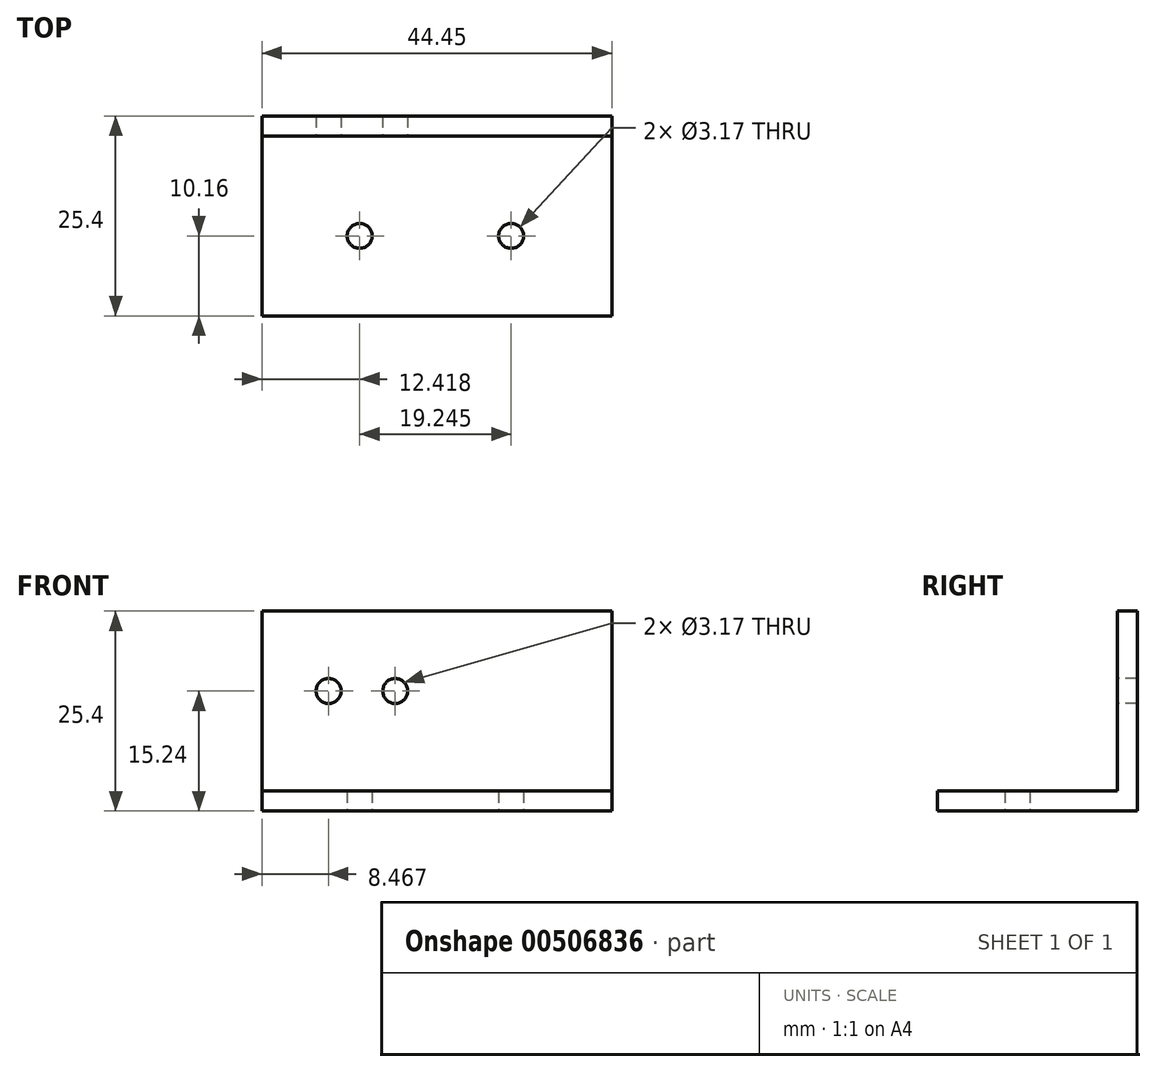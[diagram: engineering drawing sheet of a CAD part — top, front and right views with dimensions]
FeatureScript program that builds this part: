
annotation { "Feature Type Name" : "Feature", "Feature Type Description" : "" }
export const myFeature = defineFeature(function(context is Context, id is Id, definition is map)
    precondition{}
    {
        {
            var Q0;
            Q0=qCreatedBy(makeId("Top.planeOp"),FACE);
            var sketch = newSketch(context, id + "F0", { "sketchPlane" : qUnion([Q0])});
            skLineSegment(sketch, "E0.bottom", {"start": v(-44.45, -10.28) * mm, "end": v(0, -10.28) * mm});
            skLineSegment(sketch, "E0.top", {"start": v(-44.45, -35.68) * mm, "end": v(0, -35.68) * mm});
            skLineSegment(sketch, "E0.left", {"start": v(-44.45, -10.28) * mm, "end": v(-44.45, -35.68) * mm});
            skLineSegment(sketch, "E0.right", {"start": v(0, -10.28) * mm, "end": v(0, -35.68) * mm});
            skSolve(sketch);
        }
        {
            var Q0;
            Q0=makeQuery(id+"F0.imprint","IMPRINT",FACE,{"disambiguationData":[TD([[makeQuery(id+"F0.imprint","IMPRINT",EDGE,{"derivedFrom":sQuery(id+"F0.wireOp",EDGE,"E0.bottom")}),-1.0]])]});
            extrude(context, id + "F1", {"entities" : qUnion([Q0]), "depth" : 25.4 * mm, "offsetDistance" : 25.4 * mm});
        }
        {
            var Q0;
            Q0=makeQuery(id+"F1.opExtrude","CAP_FACE",FACE,{"disambiguationData":[OSD([sQuery(id+"F0.wireOp",EDGE,"E0.bottom"),sQuery(id+"F0.wireOp",EDGE,"E0.top"),sQuery(id+"F0.wireOp",EDGE,"E0.left"),sQuery(id+"F0.wireOp",EDGE,"E0.right")])],"isStart":false});
            var Q1;
            Q1=makeQuery(id+"F1.opExtrude","SWEPT_FACE",FACE,{"disambiguationData":[OSD([sQuery(id+"F0.wireOp",EDGE,"E0.right")])]});
            var Q2;
            Q2=makeQuery(id+"F1.opExtrude","SWEPT_FACE",FACE,{"disambiguationData":[OSD([sQuery(id+"F0.wireOp",EDGE,"E0.top")])]});
            var Q3;
            Q3=makeQuery(id+"F1.opExtrude","SWEPT_FACE",FACE,{"disambiguationData":[OSD([sQuery(id+"F0.wireOp",EDGE,"E0.left")])]});
            shell(context, id + "F2", {"entities" : qUnion([Q0, Q1, Q2, Q3]), "thickness" : 2.54 * mm});
        }
        {
            var Q0;
            Q0=makeQuery(id+"F2.opShell","OFFSET_FACE",FACE,{"disambiguationData":[OSD([sQuery(id+"F0.wireOp",EDGE,"E0.bottom")])]});
            var sketch = newSketch(context, id + "F3", { "sketchPlane" : qUnion([Q0])});
            skPoint(sketch, "E1", {"position": v(-27.52, 15.24) * mm});
            skPoint(sketch, "E2", {"position": v(-35.98, 15.24) * mm});
            skSolve(sketch);
        }
        {
            var Q0;
            Q0=sQuery(id+"F3.wireOp",VERTEX,"E2");
            var Q1;
            Q1=sQuery(id+"F3.wireOp",VERTEX,"E1");
            var Q2;
            Q2=makeQuery(id+"F1.opExtrude","SWEPT_BODY",BODY,{"disambiguationData":[OSD([sQuery(id+"F0.wireOp",EDGE,"E0.bottom"),sQuery(id+"F0.wireOp",EDGE,"E0.top"),sQuery(id+"F0.wireOp",EDGE,"E0.left"),sQuery(id+"F0.wireOp",EDGE,"E0.right")])]});
            hole(context, id + "F4", {"style" : HoleStyle.SIMPLE, "endStyle" : HoleEndStyle.THROUGH, "holeDiameter" : 3.17 * mm, "majorDiameter" : 6.35 * mm, "isTappedThrough" : true, "tappedDepth" : 12.7 * mm, "tapClearance" : 3, "locations" : qUnion([Q0, Q1]), "scope" : qUnion([Q2])});
        }
        {
            var Q0;
            Q0=makeQuery(id+"F1.opExtrude","CAP_FACE",FACE,{"disambiguationData":[OSD([sQuery(id+"F0.wireOp",EDGE,"E0.bottom"),sQuery(id+"F0.wireOp",EDGE,"E0.top"),sQuery(id+"F0.wireOp",EDGE,"E0.left"),sQuery(id+"F0.wireOp",EDGE,"E0.right")])],"isStart":true});
            var sketch = newSketch(context, id + "F5", { "sketchPlane" : qUnion([Q0])});
            skPoint(sketch, "E3", {"position": v(-12.79, 25.52) * mm});
            skPoint(sketch, "E4", {"position": v(-32.03, 25.52) * mm});
            skSolve(sketch);
        }
        {
            var Q0;
            Q0=sQuery(id+"F5.wireOp",VERTEX,"E3");
            var Q1;
            Q1=sQuery(id+"F5.wireOp",VERTEX,"E4");
            var Q2;
            Q2=makeQuery(id+"F1.opExtrude","SWEPT_BODY",BODY,{"disambiguationData":[OSD([sQuery(id+"F0.wireOp",EDGE,"E0.bottom"),sQuery(id+"F0.wireOp",EDGE,"E0.top"),sQuery(id+"F0.wireOp",EDGE,"E0.left"),sQuery(id+"F0.wireOp",EDGE,"E0.right")])]});
            hole(context, id + "F6", {"style" : HoleStyle.SIMPLE, "endStyle" : HoleEndStyle.THROUGH, "holeDiameter" : 3.17 * mm, "majorDiameter" : 6.35 * mm, "isTappedThrough" : true, "tappedDepth" : 12.7 * mm, "tapClearance" : 3, "locations" : qUnion([Q0, Q1]), "scope" : qUnion([Q2])});
        }
    });
